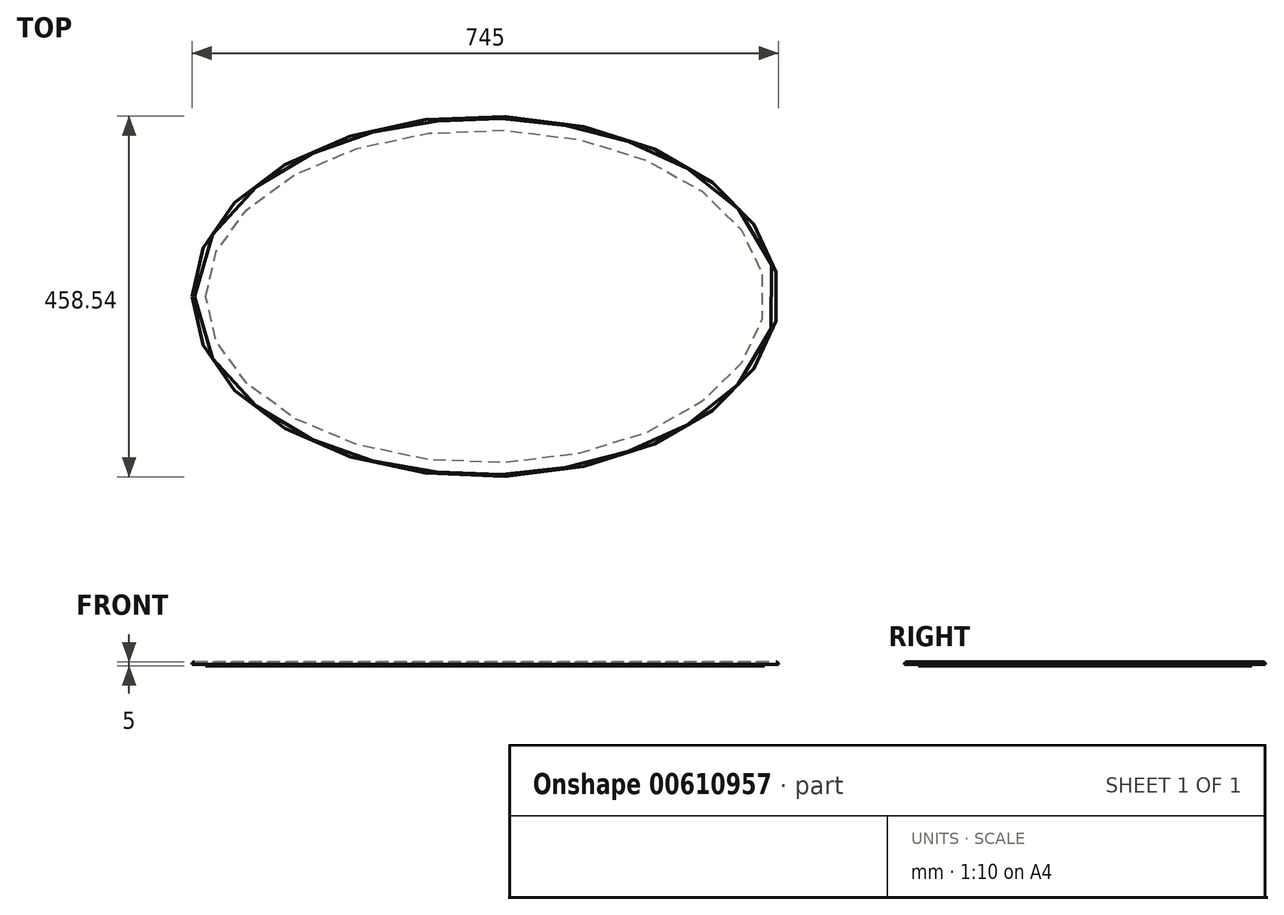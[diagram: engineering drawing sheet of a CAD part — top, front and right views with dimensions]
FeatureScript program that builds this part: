
annotation { "Feature Type Name" : "Feature", "Feature Type Description" : "" }
export const myFeature = defineFeature(function(context is Context, id is Id, definition is map)
    precondition{}
    {
        {
            var Q0;
            Q0=qCreatedBy(makeId("Top.planeOp"),FACE);
            var sketch = newSketch(context, id + "F0", { "sketchPlane" : qUnion([Q0])});
            skEllipse(sketch, "E0", {"center": v(0, 0) * mm, "majorRadius": 372.5 * mm, "minorRadius": 229.27 * mm, "majorAxis": v(-1, 0)});
            skSolve(sketch);
        }
        {
            var Q0;
            Q0 = qSketchRegion(id + "F0", true);
            extrude(context, id + "F1", {"entities" : qUnion([Q0]), "depth" : 3 * mm, "offsetDistance" : 25 * mm});
        }
        {
            var Q0;
            Q0=makeQuery(id+"F1.opExtrude","CAP_EDGE",EDGE,{"disambiguationData":[OSD([sQuery(id+"F0.wireOp",EDGE,"E0")])],"isStart":false});
            fillet(context, id + "F2", {"entities" : qUnion([Q0]), "radius" : 3 * mm, "tangentPropagation" : true, "allowEdgeOverflow" : false});
        }
        {
            var Q0;
            Q0=makeQuery(id+"F1.opExtrude","CAP_FACE",FACE,{"disambiguationData":[OSD([sQuery(id+"F0.wireOp",EDGE,"E0")])],"isStart":true});
            var sketch = newSketch(context, id + "F3", { "sketchPlane" : qUnion([Q0])});
            skEllipse(sketch, "E1", {"center": v(0, 0) * mm, "majorRadius": 355 * mm, "minorRadius": 211.77 * mm, "majorAxis": v(-1, 0)});
            skSolve(sketch);
        }
        {
            var Q0;
            Q0 = qSketchRegion(id + "F3", true);
            extrude(context, id + "F4", {"entities" : qUnion([Q0]), "operationType" : NewBodyOperationType.ADD, "depth" : 2 * mm, "offsetDistance" : 25 * mm});
        }
    });
